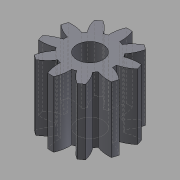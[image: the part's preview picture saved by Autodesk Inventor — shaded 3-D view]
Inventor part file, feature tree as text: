
AUTODESK INVENTOR PART (.ipt)
format: ipt  version: 2015 (Build 190159000, 159)  size: 198,656 bytes
history: native  units: mm (DEFAULTED — no unit token found)
features: plane x3, other x3, sketch x3, extrude x2
ambient origin geometry x8: Origin, YZ Plane, XZ Plane, XY Plane, X Axis, Y Axis, Z Axis, Center Point
bodies: Solid1 (feature_tree)
feature tree (11):
  extrude  "Extrusion1"  Depth=5.0mm TaperAngle=0.0deg
  plane  "Work Plane2"
  plane  "Work Plane8"
  plane  "Work Plane9"
  other  "Spur Gear"
  extrude  "Extrusion2"  Depth=10.0mm TaperAngle=0.0deg
  sketch  "Sketch1"  dims[d0=6.0mm d1=5.0mm d2=0.0mm]
  sketch  "Sketch2"  dims[d3=5.0mm d4=10.0mm d5=0.0mm]
  other  "Srf1"
  sketch  "Sketch3"  dims[d16=12.0mm d17=0.0mm d34=3.141593mm d39=0.0mm d41=0.0mm d43=12.0mm d46=12.0mm d47=0.0mm d48=0.0mm d49=2.0mm d50=10.0mm d51=0.0mm]
  other  "Pitch Diameter"
